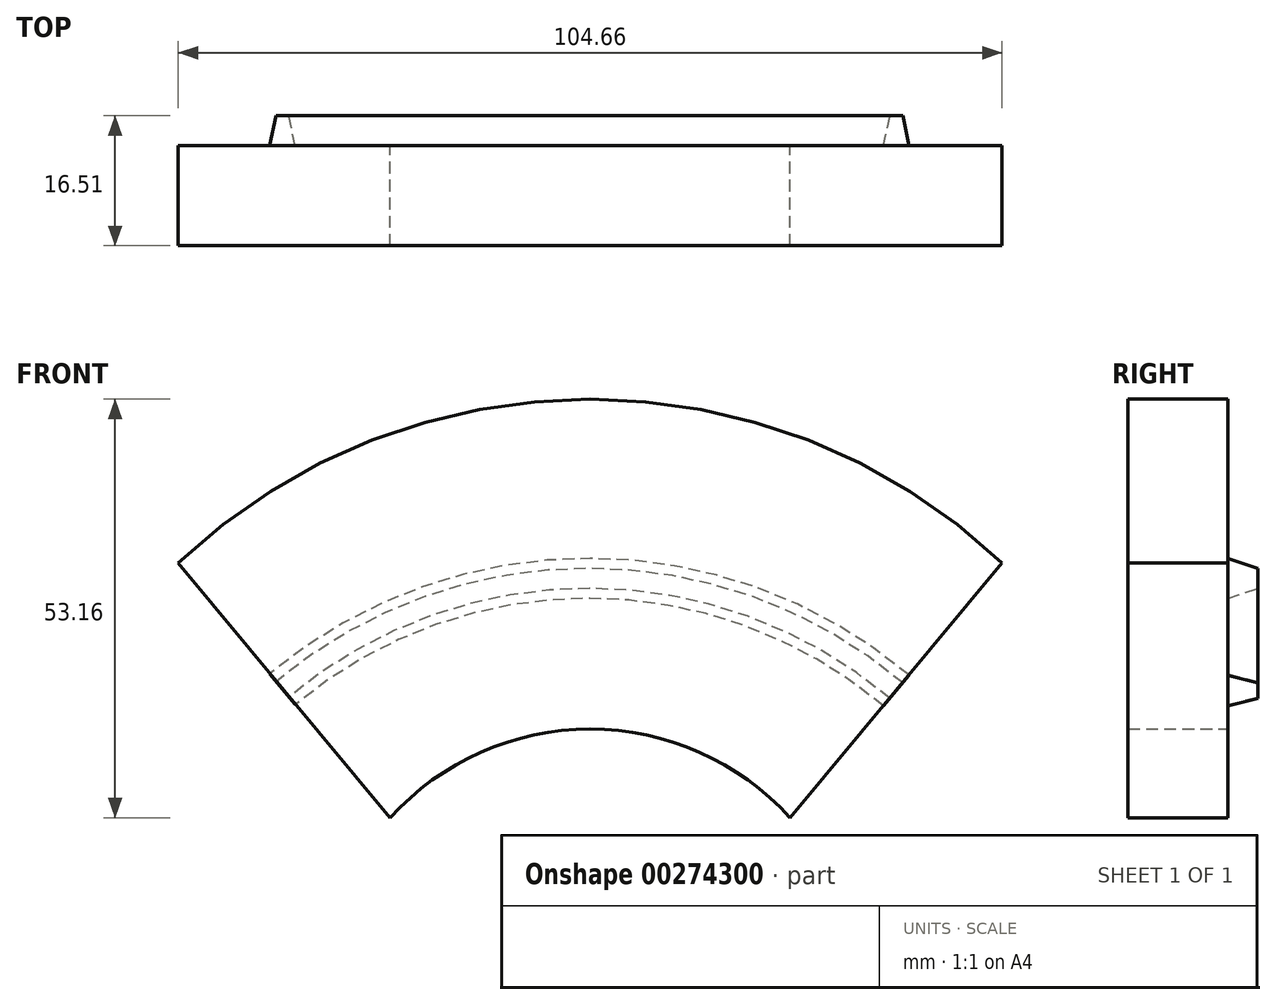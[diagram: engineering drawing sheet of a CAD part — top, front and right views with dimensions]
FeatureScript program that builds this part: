
annotation { "Feature Type Name" : "Feature", "Feature Type Description" : "" }
export const myFeature = defineFeature(function(context is Context, id is Id, definition is map)
    precondition{}
    {
        {
            var Q0;
            Q0=qCreatedBy(makeId("Front.planeOp"),FACE);
            var sketch = newSketch(context, id + "F0", { "sketchPlane" : qUnion([Q0])});
            skLineSegment(sketch, "E0", {"start": v(0, 0) * mm, "end": v(25.4, 0) * mm});
            skLineSegment(sketch, "E1", {"start": v(0, 0) * mm, "end": v(-25.4, 0) * mm});
            skArc(sketch, "E2", {"start": v(25.4, 0) * mm, "mid": v(0, 11.25) * mm, "end": v(-25.4, 0) * mm});
            skLineSegment(sketch, "E3", {"start": v(-25.4, 0) * mm, "end": v(-57.9, 39.04) * mm});
            skLineSegment(sketch, "E4", {"start": v(25.4, 0) * mm, "end": v(57.9, 39.04) * mm});
            skArc(sketch, "E5", {"start": v(-52.33, 32.35) * mm, "mid": v(0, 53.16) * mm, "end": v(52.33, 32.35) * mm});
            skSolve(sketch);
        }
        {
            var Q0;
            {var subQ0=sQuery(id+"F0.wireOp",EDGE,"E2");Q0=makeQuery(id+"F0.imprint","IMPRINT",FACE,{"disambiguationData":[TD([[makeQuery(id+"F0.imprint","IMPRINT",EDGE,{"derivedFrom":subQ0}),-1.0]])]});}
            extrude(context, id + "F1", {"entities" : qUnion([Q0]), "depth" : 12.7 * mm});
        }
        {
            var Q0;
            Q0=qCreatedBy(makeId("Front.planeOp"),FACE);
            var sketch = newSketch(context, id + "F2", { "sketchPlane" : qUnion([Q0])});
            skArc(sketch, "E6", {"start": v(40.66, 18.28) * mm, "mid": v(-0.08, 33.17) * mm, "end": v(-40.87, 18.43) * mm});
            skSolve(sketch);
        }
        {
            var Q0;
            Q0=makeQuery(id+"F1.opExtrude","SWEPT_FACE",FACE,{"disambiguationData":[OSD([sQuery(id+"F0.wireOp",EDGE,"E4")])]});
            var sketch = newSketch(context, id + "F3", { "sketchPlane" : qUnion([Q0])});
            skLineSegment(sketch, "E7", {"start": v(0, 37.3) * mm, "end": v(0, 39.84) * mm});
            skLineSegment(sketch, "E8", {"start": v(0, 37.3) * mm, "end": v(0, 34.76) * mm});
            skLineSegment(sketch, "E9", {"start": v(0, 37.3) * mm, "end": v(3.81, 37.3) * mm});
            skLineSegment(sketch, "E10", {"start": v(3.81, 37.3) * mm, "end": v(3.81, 38.57) * mm});
            skLineSegment(sketch, "E11", {"start": v(3.81, 37.3) * mm, "end": v(3.81, 36.03) * mm});
            skLineSegment(sketch, "E12", {"start": v(0, 34.76) * mm, "end": v(3.81, 36.03) * mm});
            skLineSegment(sketch, "E13", {"start": v(0, 39.84) * mm, "end": v(3.8, 38.57) * mm});
            skPoint(sketch, "E14", {"position": v(0, 37.3) * mm});
            skSolve(sketch);
        }
        {
            var Q0;
            Q0=makeQuery(id+"F3.imprint","IMPRINT",FACE,{"disambiguationData":[TD([[makeQuery(id+"F3.imprint","IMPRINT",EDGE,{"derivedFrom":sQuery(id+"F3.wireOp",EDGE,"E7")}),-1.0]])]});
            var Q1;
            Q1=makeQuery(id+"F3.imprint","IMPRINT",FACE,{"disambiguationData":[TD([[makeQuery(id+"F3.imprint","IMPRINT",EDGE,{"derivedFrom":sQuery(id+"F3.wireOp",EDGE,"E8")}),-1.0]])]});
            var Q2;
            Q2=sQuery(id+"F2.wireOp",EDGE,"E6");
            sweep(context, id + "F4", {"operationType" : NewBodyOperationType.ADD, "profiles" : qUnion([Q0, Q1]), "path" : qUnion([Q2])});
        }
    });
